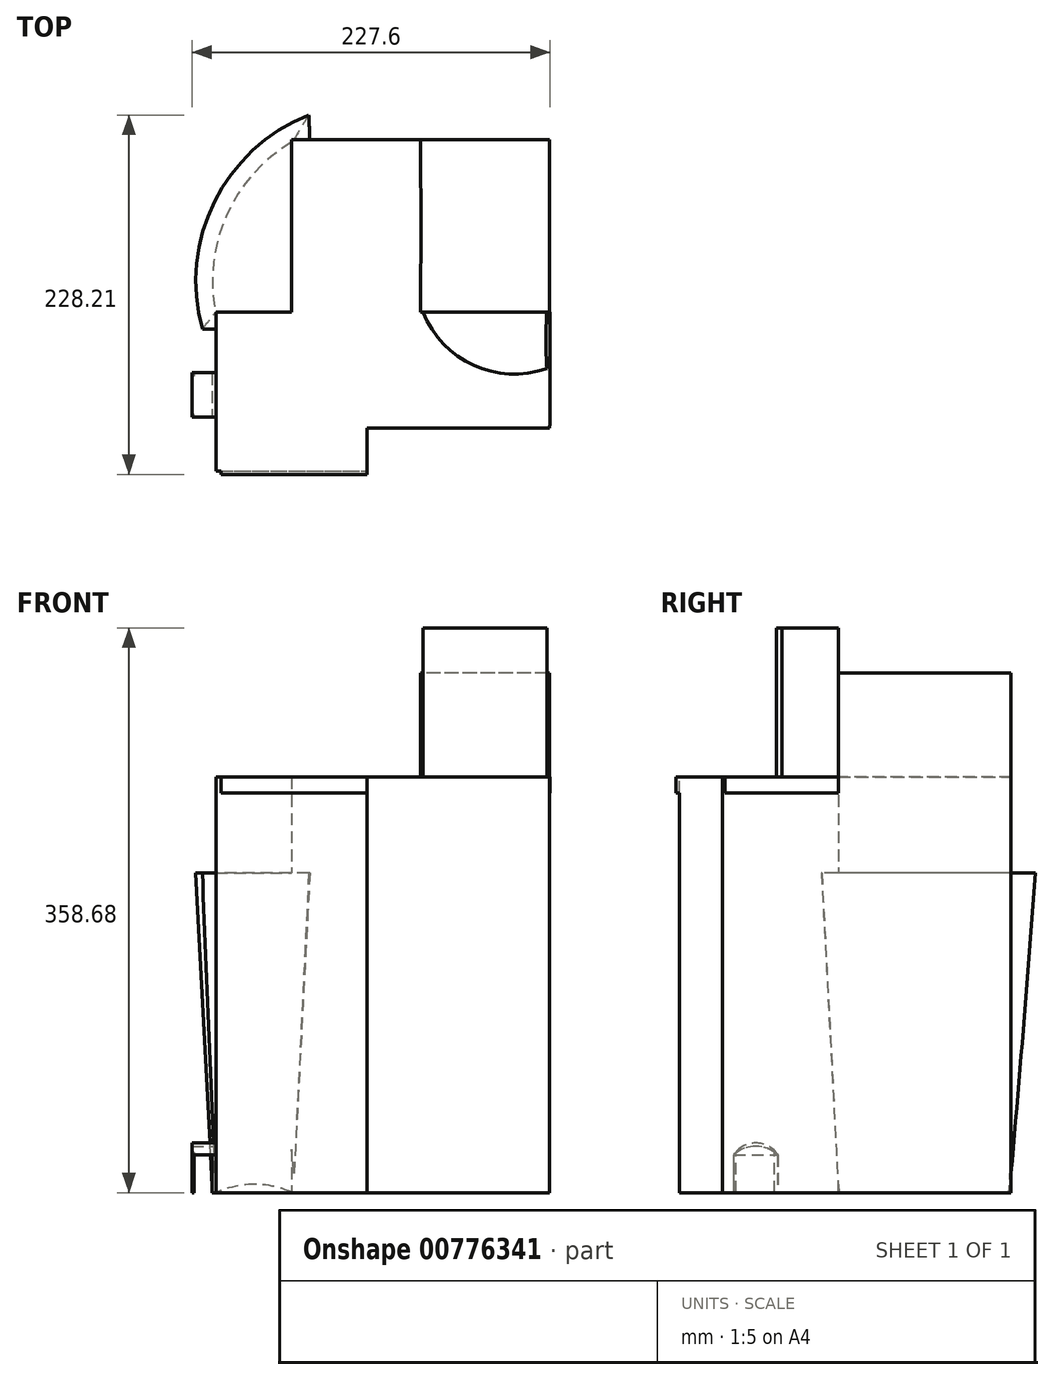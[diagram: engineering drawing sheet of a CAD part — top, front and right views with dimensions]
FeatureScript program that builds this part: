
annotation { "Feature Type Name" : "Feature", "Feature Type Description" : "" }
export const myFeature = defineFeature(function(context is Context, id is Id, definition is map)
    precondition{}
    {
        {
            var Q0;
            Q0=qCreatedBy(makeId("Top.planeOp"),FACE);
            var sketch = newSketch(context, id + "F0", { "sketchPlane" : qUnion([Q0])});
            skLineSegment(sketch, "E0.bottom", {"start": v(115.7, 109.61) * mm, "end": v(0, 109.61) * mm});
            skLineSegment(sketch, "E0.top", {"start": v(115.7, -73.6) * mm, "end": v(0, -73.6) * mm});
            skLineSegment(sketch, "E0.left", {"start": v(115.7, 109.61) * mm, "end": v(115.7, -73.6) * mm});
            skLineSegment(sketch, "E0.right", {"start": v(0, 109.61) * mm, "end": v(0, -73.6) * mm});
            skLineSegment(sketch, "E1.bottom", {"start": v(-95.97, 0) * mm, "end": v(0, 0) * mm});
            skLineSegment(sketch, "E1.top", {"start": v(-95.97, -101) * mm, "end": v(0, -101) * mm});
            skLineSegment(sketch, "E1.left", {"start": v(-95.97, 0) * mm, "end": v(-95.97, -101) * mm});
            skLineSegment(sketch, "E1.right", {"start": v(0, 0) * mm, "end": v(0, -101) * mm});
            skLineSegment(sketch, "E2.bottom", {"start": v(63.61, 0) * mm, "end": v(0, 0) * mm});
            skLineSegment(sketch, "E2.top", {"start": v(63.61, 77.25) * mm, "end": v(0, 77.25) * mm});
            skLineSegment(sketch, "E2.left", {"start": v(63.61, 0) * mm, "end": v(63.61, 77.25) * mm});
            skLineSegment(sketch, "E2.right", {"start": v(0, 0) * mm, "end": v(0, 77.25) * mm});
            skPoint(sketch, "E3.firstSnap0", {"position": v(-47.99, 0) * mm});
            skLineSegment(sketch, "E3.bottom", {"start": v(-47.99, 109.61) * mm, "end": v(0, 109.61) * mm});
            skLineSegment(sketch, "E3.top", {"start": v(-47.99, 0) * mm, "end": v(0, 0) * mm});
            skLineSegment(sketch, "E3.left", {"start": v(-47.99, 109.61) * mm, "end": v(-47.99, 0) * mm});
            skLineSegment(sketch, "E3.right", {"start": v(0, 109.61) * mm, "end": v(0, 0) * mm});
            skSolve(sketch);
        }
        {
            var Q0;
            {var subQ4=sQuery(id+"F0.wireOp",EDGE,"E0.bottom");Q0=makeQuery(id+"F0.imprint","IMPRINT",FACE,{"disambiguationData":[TD([[makeQuery(id+"F0.imprint","IMPRINT",EDGE,{"derivedFrom":subQ4}),1.0]])]});}
            var Q1;
            {var subQ0=sQuery(id+"F0.wireOp",EDGE,"E2.bottom");Q1=makeQuery(id+"F0.imprint","IMPRINT",FACE,{"disambiguationData":[TD([[makeQuery(id+"F0.imprint","IMPRINT",EDGE,{"derivedFrom":subQ0}),-1.0]])]});}
            var Q2;
            {var subQ1=sQuery(id+"F0.wireOp",EDGE,"E3.bottom");Q2=makeQuery(id+"F0.imprint","IMPRINT",FACE,{"disambiguationData":[TD([[makeQuery(id+"F0.imprint","IMPRINT",EDGE,{"derivedFrom":subQ1}),-1.0]])]});}
            var Q3;
            Q3=makeQuery(id+"F0.imprint","IMPRINT",FACE,{"disambiguationData":[TD([[makeQuery(id+"F0.imprint","IMPRINT",EDGE,{"derivedFrom":sQuery(id+"F0.wireOp",EDGE,"E1.bottom")}),-1.0]])]});
            extrude(context, id + "F1", {"entities" : qUnion([Q0, Q1, Q2, Q3]), "depth" : 254 * mm, "offsetDistance" : 25.4 * mm});
        }
        {
            var Q0;
            Q0=qCreatedBy(makeId("Top.planeOp"),FACE);
            var sketch = newSketch(context, id + "F2", { "sketchPlane" : qUnion([Q0])});
            skArc(sketch, "E4", {"start": v(-46.97, 108.54) * mm, "mid": v(-89, 62.16) * mm, "end": v(-96.27, 0) * mm});
            skArc(sketch, "E5", {"start": v(-46.97, 0) * mm, "mid": v(-45.94, 54.27) * mm, "end": v(-46.97, 108.54) * mm});
            skArc(sketch, "E6", {"start": v(-46.97, 0) * mm, "mid": v(-71.62, 0.27) * mm, "end": v(-96.27, 0) * mm});
            skSolve(sketch);
        }
        {
            var Q0;
            Q0=makeQuery(id+"F2.imprint","IMPRINT",FACE,{"disambiguationData":[TD([[makeQuery(id+"F2.imprint","IMPRINT",EDGE,{"derivedFrom":sQuery(id+"F2.wireOp",EDGE,"E4")}),1.0]])]});
            extrude(context, id + "F3", {"entities" : qUnion([Q0]), "operationType" : NewBodyOperationType.ADD, "depth" : 203.2 * mm, "offsetDistance" : 25.4 * mm, "hasDraft" : true, "draftAngle" : 3 * degree});
        }
        {
            var Q0;
            Q0=makeQuery(id+"F1.opExtrude","SWEPT_FACE",FACE,{"disambiguationData":[OSD([sQuery(id+"F0.wireOp",EDGE,"E0.bottom"),sQuery(id+"F0.wireOp",EDGE,"E3.bottom")])]});
            var sketch = newSketch(context, id + "F4", { "sketchPlane" : qUnion([Q0])});
            skLineSegment(sketch, "E7.bottom", {"start": v(0, 27.53) * mm, "end": v(23.92, 27.53) * mm});
            skLineSegment(sketch, "E7.top", {"start": v(0, 0) * mm, "end": v(23.92, 0) * mm});
            skLineSegment(sketch, "E7.left", {"start": v(0, 27.53) * mm, "end": v(0, 0) * mm});
            skLineSegment(sketch, "E7.right", {"start": v(23.92, 27.53) * mm, "end": v(23.92, 0) * mm});
            skSolve(sketch);
        }
        {
            var Q0;
            Q0=makeQuery(id+"F4.imprint","IMPRINT",FACE,{"disambiguationData":[TD([[makeQuery(id+"F4.imprint","IMPRINT",EDGE,{"derivedFrom":sQuery(id+"F4.wireOp",EDGE,"E7.bottom")}),-1.0]])]});
            extrude(context, id + "F5", {"entities" : qUnion([Q0]), "operationType" : NewBodyOperationType.ADD, "oppositeDirection" : true, "depth" : 50.8 * mm, "offsetDistance" : 25.4 * mm});
        }
        {
            var Q0;
            Q0=makeQuery(id+"F1.opExtrude","CAP_FACE",FACE,{"disambiguationData":[OSD([sQuery(id+"F0.wireOp",EDGE,"E0.bottom"),sQuery(id+"F0.wireOp",EDGE,"E0.top"),sQuery(id+"F0.wireOp",EDGE,"E0.left"),sQuery(id+"F0.wireOp",EDGE,"E1.bottom"),sQuery(id+"F0.wireOp",EDGE,"E1.top"),sQuery(id+"F0.wireOp",EDGE,"E1.left"),sQuery(id+"F0.wireOp",EDGE,"E1.right"),sQuery(id+"F0.wireOp",EDGE,"E3.bottom"),sQuery(id+"F0.wireOp",EDGE,"E3.left")])],"isStart":false});
            var sketch = newSketch(context, id + "F6", { "sketchPlane" : qUnion([Q0])});
            skPoint(sketch, "E8.firstSnap0", {"position": v(33.85, 109.61) * mm});
            skLineSegment(sketch, "E8.bottom", {"start": v(33.85, 0) * mm, "end": v(115.7, 0) * mm});
            skLineSegment(sketch, "E8.top", {"start": v(33.85, 109.61) * mm, "end": v(115.7, 109.61) * mm});
            skLineSegment(sketch, "E8.left", {"start": v(33.85, 0) * mm, "end": v(33.85, 109.61) * mm});
            skLineSegment(sketch, "E8.right", {"start": v(115.7, 0) * mm, "end": v(115.7, 109.61) * mm});
            skArc(sketch, "E9", {"start": v(33.85, 109.61) * mm, "mid": v(6.42, 54.8) * mm, "end": v(33.85, 0) * mm});
            skArc(sketch, "E10", {"start": v(33.85, 0) * mm, "mid": v(34.15, 54.8) * mm, "end": v(33.85, 109.61) * mm});
            skSolve(sketch);
        }
        {
            var Q0;
            Q0=makeQuery(id+"F6.imprint","IMPRINT",FACE,{"disambiguationData":[TD([[makeQuery(id+"F6.imprint","IMPRINT",EDGE,{"derivedFrom":sQuery(id+"F6.wireOp",EDGE,"E8.bottom")}),1.0]])]});
            extrude(context, id + "F7", {"entities" : qUnion([Q0]), "operationType" : NewBodyOperationType.ADD, "depth" : 76.2 * mm, "offsetDistance" : 25.4 * mm});
        }
        {
            var Q0;
            Q0=makeQuery(id+"F1.opExtrude","CAP_FACE",FACE,{"disambiguationData":[OSD([sQuery(id+"F0.wireOp",EDGE,"E0.bottom"),sQuery(id+"F0.wireOp",EDGE,"E0.top"),sQuery(id+"F0.wireOp",EDGE,"E0.left"),sQuery(id+"F0.wireOp",EDGE,"E1.bottom"),sQuery(id+"F0.wireOp",EDGE,"E1.top"),sQuery(id+"F0.wireOp",EDGE,"E1.left"),sQuery(id+"F0.wireOp",EDGE,"E1.right"),sQuery(id+"F0.wireOp",EDGE,"E3.bottom"),sQuery(id+"F0.wireOp",EDGE,"E3.left")])],"isStart":false});
            var sketch = newSketch(context, id + "F8", { "sketchPlane" : qUnion([Q0])});
            skSolve(sketch);
        }
        {
            var Q0;
            Q0=makeQuery(id+"F8.imprint","IMPRINT",FACE,{"disambiguationData":[TD([[makeQuery(id+"F8.imprint","IMPRINT",EDGE,{"derivedFrom":makeQuery(id+"F1.opExtrude","CAP_EDGE",EDGE,{"disambiguationData":[OSD([sQuery(id+"F0.wireOp",EDGE,"E0.top")])],"isStart":false})}),-1.0]])]});
            var sketch = newSketch(context, id + "F9", { "sketchPlane" : qUnion([Q0])});
            skArc(sketch, "E11", {"start": v(35.62, 0) * mm, "mid": v(67.67, -33.7) * mm, "end": v(114.12, -35.8) * mm});
            skArc(sketch, "E12", {"start": v(114.12, 0) * mm, "mid": v(113.67, -17.9) * mm, "end": v(114.12, -35.8) * mm});
            skArc(sketch, "E13", {"start": v(114.12, 0) * mm, "mid": v(74.87, 0.08) * mm, "end": v(35.62, 0) * mm});
            skSolve(sketch);
        }
        {
            var Q0;
            {var subQ0=sQuery(id+"F9.wireOp",EDGE,"E11");Q0=makeQuery(id+"F9.imprint","IMPRINT",FACE,{"disambiguationData":[TD([[makeQuery(id+"F9.imprint","IMPRINT",EDGE,{"derivedFrom":subQ0}),1.0]])]});}
            var Q1;
            Q1 = qSketchRegion(id + "F9", true);
            extrude(context, id + "F10", {"entities" : qUnion([Q0, Q1]), "operationType" : NewBodyOperationType.ADD, "depth" : 104.68 * mm, "offsetDistance" : 25.4 * mm});
        }
        {
            var Q0;
            Q0=makeQuery(id+"F8.imprint","IMPRINT",FACE,{"disambiguationData":[TD([[makeQuery(id+"F8.imprint","IMPRINT",EDGE,{"derivedFrom":makeQuery(id+"F1.opExtrude","CAP_EDGE",EDGE,{"disambiguationData":[OSD([sQuery(id+"F0.wireOp",EDGE,"E0.top")])],"isStart":false})}),-1.0]])]});
            var sketch = newSketch(context, id + "F11", { "sketchPlane" : qUnion([Q0])});
            skLineSegment(sketch, "E14", {"start": v(116.34, -37.6) * mm, "end": v(116.34, -71.99) * mm});
            skLineSegment(sketch, "E15", {"start": v(116.34, -71.99) * mm, "end": v(0, -71.99) * mm});
            skLineSegment(sketch, "E16", {"start": v(0, -71.99) * mm, "end": v(0, -103.08) * mm});
            skLineSegment(sketch, "E17", {"start": v(0, -103.08) * mm, "end": v(-92.7, -103.08) * mm});
            skLineSegment(sketch, "E18", {"start": v(-92.7, -103.08) * mm, "end": v(-92.7, 0) * mm});
            skLineSegment(sketch, "E19", {"start": v(-92.7, 0) * mm, "end": v(-47.96, 0) * mm});
            skLineSegment(sketch, "E20", {"start": v(-47.96, 0) * mm, "end": v(-47.96, 107.78) * mm});
            skLineSegment(sketch, "E21", {"start": v(-47.96, 107.78) * mm, "end": v(31.5, 107.78) * mm});
            skLineSegment(sketch, "E22", {"start": v(31.5, 107.78) * mm, "end": v(31.5, 0) * mm});
            skLineSegment(sketch, "E23", {"start": v(31.5, 0) * mm, "end": v(116.34, 0) * mm});
            skLineSegment(sketch, "E24", {"start": v(116.34, 0) * mm, "end": v(116.34, -37.6) * mm});
            skSolve(sketch);
        }
        {
            var Q0;
            Q0=makeQuery(id+"F8.imprint","IMPRINT",FACE,{"disambiguationData":[TD([[makeQuery(id+"F8.imprint","IMPRINT",EDGE,{"derivedFrom":makeQuery(id+"F1.opExtrude","CAP_EDGE",EDGE,{"disambiguationData":[OSD([sQuery(id+"F0.wireOp",EDGE,"E0.top")])],"isStart":false})}),-1.0]])]});
            var Q1;
            Q1 = qSketchRegion(id + "F11", true);
            extrude(context, id + "F12", {"entities" : qUnion([Q0, Q1]), "operationType" : NewBodyOperationType.ADD, "depth" : 10 * mm, "offsetDistance" : 25.4 * mm});
        }
        {
            var Q0;
            {var subQ0=sQuery(id+"F0.wireOp",EDGE,"E1.left");Q0=makeQuery(id+"F12.boolean.opBoolean","MERGE",FACE,{"derivedFrom":[makeQuery(id+"F1.opExtrude","SWEPT_FACE",FACE,{"disambiguationData":[OSD([subQ0])]}),makeQuery(id+"F12.opExtrude","SWEPT_FACE",FACE,{"disambiguationData":[OSD([subQ0])]})]});}
            var sketch = newSketch(context, id + "F13", { "sketchPlane" : qUnion([Q0])});
            skLineSegment(sketch, "E25", {"start": v(66.53, 0) * mm, "end": v(66.53, 23.9) * mm});
            skLineSegment(sketch, "E26", {"start": v(66.53, 23.9) * mm, "end": v(38.66, 23.9) * mm});
            skLineSegment(sketch, "E27", {"start": v(38.66, 23.9) * mm, "end": v(38.66, 0) * mm});
            skLineSegment(sketch, "E28", {"start": v(38.66, 0) * mm, "end": v(66.53, 0) * mm});
            skSolve(sketch);
        }
        {
            var Q0;
            Q0=makeQuery(id+"F13.imprint","IMPRINT",FACE,{"disambiguationData":[TD([[makeQuery(id+"F13.imprint","IMPRINT",EDGE,{"derivedFrom":sQuery(id+"F13.wireOp",EDGE,"E25")}),1.0]])]});
            var sketch = newSketch(context, id + "F14", { "sketchPlane" : qUnion([Q0])});
            skLineSegment(sketch, "E29", {"start": v(53.23, 23.76) * mm, "end": v(53.23, 0) * mm});
            skSolve(sketch);
        }
        {
            var Q0;
            {var subQ22=sQuery(id+"F13.wireOp",EDGE,"E25");Q0=makeQuery(id+"F13.imprint","IMPRINT",FACE,{"disambiguationData":[TD([[makeQuery(id+"F13.imprint","IMPRINT",EDGE,{"derivedFrom":subQ22}),-1.0]])]});}
            var sketch = newSketch(context, id + "F15", { "sketchPlane" : qUnion([Q0])});
            skArc(sketch, "E30", {"start": v(66.63, 24.05) * mm, "mid": v(52.5, 31.54) * mm, "end": v(38.43, 23.93) * mm});
            skArc(sketch, "E31", {"start": v(66.63, 24.05) * mm, "mid": v(52.5, 29.46) * mm, "end": v(38.43, 23.93) * mm});
            skSolve(sketch);
        }
        {
            var Q0;
            Q0=makeQuery(id+"F15.imprint","IMPRINT",FACE,{"disambiguationData":[TD([[makeQuery(id+"F15.imprint","IMPRINT",EDGE,{"derivedFrom":sQuery(id+"F15.wireOp",EDGE,"E30")}),1.0]])]});
            extrude(context, id + "F16", {"entities" : qUnion([Q0]), "operationType" : NewBodyOperationType.ADD, "depth" : 15.29 * mm, "offsetDistance" : 25.4 * mm});
        }
        {
            var Q0;
            Q0=makeQuery(id+"F16.opExtrude","CAP_FACE",FACE,{"disambiguationData":[OSD([sQuery(id+"F15.wireOp",EDGE,"E30"),sQuery(id+"F15.wireOp",EDGE,"E31")])],"isStart":false});
            var sketch = newSketch(context, id + "F17", { "sketchPlane" : qUnion([Q0])});
            skLineSegment(sketch, "E32.bottom", {"start": v(38.43, 23.93) * mm, "end": v(38.43, 23.93) * mm});
            skLineSegment(sketch, "E32.top", {"start": v(38.43, 0) * mm, "end": v(38.43, 0) * mm});
            skLineSegment(sketch, "E32.left", {"start": v(38.43, 23.93) * mm, "end": v(38.43, 0) * mm});
            skLineSegment(sketch, "E32.right", {"start": v(38.43, 23.93) * mm, "end": v(38.43, 0) * mm});
            skLineSegment(sketch, "E33.bottom", {"start": v(38.43, 0) * mm, "end": v(40.55, 0) * mm});
            skLineSegment(sketch, "E33.top", {"start": v(38.43, 25.64) * mm, "end": v(40.55, 25.64) * mm});
            skLineSegment(sketch, "E33.left", {"start": v(38.43, 0) * mm, "end": v(38.43, 25.64) * mm});
            skLineSegment(sketch, "E33.right", {"start": v(40.55, 0) * mm, "end": v(40.55, 25.64) * mm});
            skLineSegment(sketch, "E34.bottom", {"start": v(40.55, 0) * mm, "end": v(38.43, 0) * mm});
            skLineSegment(sketch, "E34.top", {"start": v(40.55, 0) * mm, "end": v(38.43, 0) * mm});
            skLineSegment(sketch, "E34.left", {"start": v(40.55, 0) * mm, "end": v(40.55, 0) * mm});
            skLineSegment(sketch, "E35.bottom", {"start": v(66.63, 24.05) * mm, "end": v(66.63, 24.05) * mm});
            skLineSegment(sketch, "E35.top", {"start": v(66.63, 0) * mm, "end": v(66.63, 0) * mm});
            skLineSegment(sketch, "E35.left", {"start": v(66.63, 24.05) * mm, "end": v(66.63, 0) * mm});
            skLineSegment(sketch, "E35.right", {"start": v(66.63, 24.05) * mm, "end": v(66.63, 0) * mm});
            skLineSegment(sketch, "E36.bottom", {"start": v(66.63, 0) * mm, "end": v(65.06, 0) * mm});
            skLineSegment(sketch, "E36.top", {"start": v(66.63, 25.34) * mm, "end": v(65.06, 25.34) * mm});
            skLineSegment(sketch, "E36.left", {"start": v(66.63, 0) * mm, "end": v(66.63, 25.34) * mm});
            skLineSegment(sketch, "E36.right", {"start": v(65.06, 0) * mm, "end": v(65.06, 25.34) * mm});
            skSolve(sketch);
        }
        {
            var Q0;
            {var subQ0=sQuery(id+"F17.wireOp",EDGE,"E36.bottom");Q0=makeQuery(id+"F17.imprint","IMPRINT",FACE,{"disambiguationData":[TD([[makeQuery(id+"F17.imprint","IMPRINT",EDGE,{"derivedFrom":subQ0}),-1.0]])]});}
            var Q1;
            {var subQ4=sQuery(id+"F17.wireOp",EDGE,"E33.right");Q1=makeQuery(id+"F17.imprint","IMPRINT",FACE,{"disambiguationData":[TD([[makeQuery(id+"F17.imprint","IMPRINT",EDGE,{"derivedFrom":subQ4}),1.0]])]});}
            extrude(context, id + "F18", {"entities" : qUnion([Q0, Q1]), "operationType" : NewBodyOperationType.ADD, "oppositeDirection" : true, "depth" : 1.4 * mm, "offsetDistance" : 25.4 * mm});
        }
        {
            var Q0;
            {var subQ1=makeQuery(id+"F13.imprint","IMPRINT",EDGE,{"derivedFrom":sQuery(id+"F13.wireOp",EDGE,"E25")});Q0=makeQuery(id+"F14.imprint","IMPRINT",FACE,{"disambiguationData":[TD([[makeQuery(id+"F14.imprint","IMPRINT",EDGE,{"derivedFrom":subQ1}),1.0]])]});}
            extrude(context, id + "F19", {"entities" : qUnion([Q0]), "operationType" : NewBodyOperationType.ADD, "depth" : 2.43 * mm, "offsetDistance" : 25.4 * mm});
        }
        {
            var Q0;
            Q0=makeQuery(id+"F19.opExtrude","CAP_FACE",FACE,{"disambiguationData":[OSD([sQuery(id+"F13.wireOp",EDGE,"E25"),sQuery(id+"F13.wireOp",EDGE,"E26"),sQuery(id+"F13.wireOp",EDGE,"E27"),sQuery(id+"F13.wireOp",EDGE,"E28")])],"isStart":false});
            var sketch = newSketch(context, id + "F20", { "sketchPlane" : qUnion([Q0])});
            skLineSegment(sketch, "E37.bottom", {"start": v(52.6, 23.9) * mm, "end": v(52.6, 23.9) * mm});
            skLineSegment(sketch, "E37.top", {"start": v(52.6, 0) * mm, "end": v(52.6, 0) * mm});
            skLineSegment(sketch, "E37.left", {"start": v(52.6, 23.9) * mm, "end": v(52.6, 0) * mm});
            skLineSegment(sketch, "E37.right", {"start": v(52.6, 23.9) * mm, "end": v(52.6, 0) * mm});
            skSolve(sketch);
        }
        {
            var Q0;
            Q0=sQuery(id+"F20.wireOp",EDGE,"E37.left");
            extrude(context, id + "F21", {"bodyType" : ToolBodyType.SURFACE, "surfaceEntities" : qUnion([Q0]), "oppositeDirection" : true, "depth" : 2.2 * mm, "offsetDistance" : 25.4 * mm});
        }
    });
